# Revit family: andho_mini_722183_0031_76_fdfc
name_source: partatom
category: Lighting Fixtures
units: mm (PartAtom-declared; Revit-internal decimal feet)

## family parameters
Cut with Voids When Loaded = No
Host = Face
Light Source = No
Part Type = Normal
Room Calculation Point = No
Round Connector Dimension = Use Diameter
Shared = No

## types (1)
- ANDHO mini (1 x LED Modul 830, 2050 lm, 3000)
    Apparent Load = 24 VA
    CIE Flux Codes = 96 99 100 100 100
    Color Rendering = 80
    Color Temperature = 3000
    Default Elevation = 1800 mm
    Description = Series: ANDHO mini
Surface-mounted LED projector in a timeless design. Housing: die-cast aluminium, seawater resistant powder-coated. Integral membrane valve for pressure compensation and avoidance of condensation. MIRO-SILVER reflectors for outstanding efficiency or polycarbonate lenses for the best uniformity of the light cone. Cover clear single-pane toughened glass, edge printed. COB LED with socket for easy replacement. Projector: horizontal rotation range: 360°, vertical swivel range: 90°. Lockable projector orientation. Driver integrated. 
Colour: anthracite metallic (DB703)
Length: 190 mm
Width: 114 mm
Height: 152 mm
Lamp: LED
System power: 24 W
Rated luminous flux: 2050 lm
Luminous efficiency: 85 lm/W
Control gear: Converter, dimmable, DALI
Protection class: II
Type of protection: IP 65
    Height = 152 mm
    Lamp = 1 x LED Modul 830
    Lamp Light Flux = 2050 lm
    Lamp count = 1
    Length = 190 mm  [stored 0.62336 ft]
    Lifetime = 50000 h
    Luminous efficacy = 85 lm/W
    Manufacturer = RZB
    ModVariant = No
    Model = 722183.0031.76
    Mounting Place = Floor
    Mounting Type = Freestanding
    Number of Poles = 1
    OnlyDefault = Yes
    Power Factor = 1
    Product Name = ANDHO mini
    Product group = Floodlights and spotlights
    ProductGroupID = 1354
    Protection Class = Protection class II
    Protection Degree = IP 65
    RLX_Detail_Level = 1
    RLX_Emergency_Light_Flux = 0 lm
    RLX_Emergency_Type = 0
    RLX_Emergency_Type_DB = No
    RlxData = <blob elided: 49849 chars, md5=0df9044b>
    Socket = socket
    Standby Power = 0 W
    System Light Flux = 2050 lm
    System Power = 24 W
    Type Comments = ALEA SPOT
    Type Image = 722183.0031.76.jpg
    URL = http://relux.com
    VarID = ---
    Voltage = 0 V
    Weight = 0.00 kg
    Width = 114 mm

note: [stored X ft] marks values corroborated as IEEE doubles in the binary element streams (Revit-internal decimal feet)

## geometry (parser evidence)
native form markers: Sweep x16
no freeform markers — native parametric forms only
